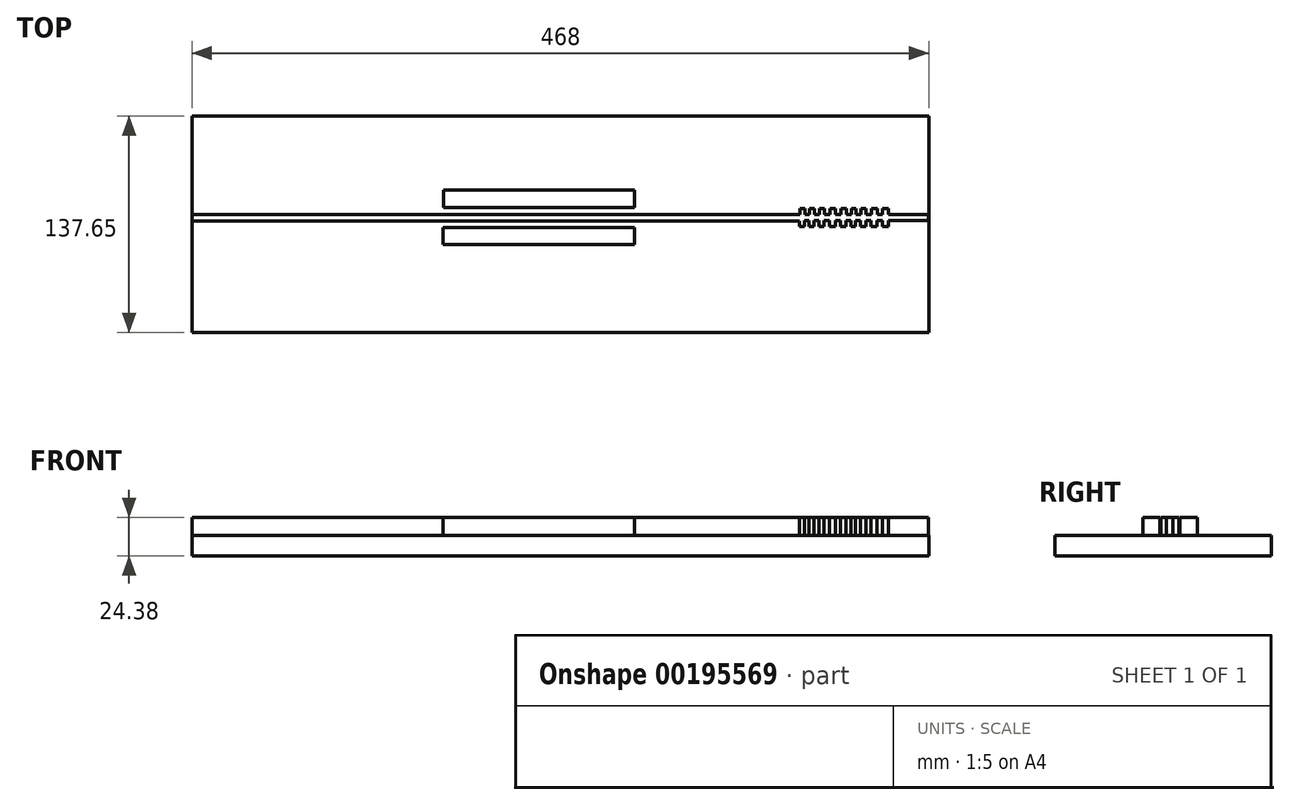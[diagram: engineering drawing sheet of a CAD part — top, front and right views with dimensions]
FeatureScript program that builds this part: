
annotation { "Feature Type Name" : "Feature", "Feature Type Description" : "" }
export const myFeature = defineFeature(function(context is Context, id is Id, definition is map)
    precondition{}
    {
        {
            var Q0;
            Q0=qCreatedBy(makeId("Top.planeOp"),FACE);
            var sketch = newSketch(context, id + "F0", { "sketchPlane" : qUnion([Q0])});
            skLineSegment(sketch, "E0.bottom", {"start": v(-262.44, -29.47) * mm, "end": v(205.56, -29.47) * mm});
            skLineSegment(sketch, "E0.top", {"start": v(-262.44, 108.18) * mm, "end": v(205.56, 108.18) * mm});
            skLineSegment(sketch, "E0.left", {"start": v(-262.44, -29.47) * mm, "end": v(-262.44, 108.18) * mm});
            skLineSegment(sketch, "E0.right", {"start": v(205.56, -29.47) * mm, "end": v(205.56, 108.18) * mm});
            skSolve(sketch);
        }
        {
            var Q0;
            Q0 = qSketchRegion(id + "F0", true);
            extrude(context, id + "F1", {"entities" : qUnion([Q0]), "depth" : 12.95 * mm});
        }
        {
            var Q0;
            Q0=makeQuery(id+"F1.opExtrude","CAP_FACE",FACE,{"disambiguationData":[OSD([sQuery(id+"F0.wireOp",EDGE,"E0.bottom"),sQuery(id+"F0.wireOp",EDGE,"E0.top"),sQuery(id+"F0.wireOp",EDGE,"E0.left"),sQuery(id+"F0.wireOp",EDGE,"E0.right")])],"isStart":false});
            var sketch = newSketch(context, id + "F2", { "sketchPlane" : qUnion([Q0])});
            skLineSegment(sketch, "E1", {"start": v(123.78, 45.55) * mm, "end": v(123.78, 49.46) * mm});
            skLineSegment(sketch, "E2", {"start": v(123.78, 49.46) * mm, "end": v(126.84, 49.46) * mm});
            skLineSegment(sketch, "E3", {"start": v(126.84, 49.46) * mm, "end": v(126.84, 45.7) * mm});
            skLineSegment(sketch, "E4", {"start": v(126.84, 45.7) * mm, "end": v(129.83, 45.7) * mm});
            skLineSegment(sketch, "E5", {"start": v(129.83, 45.7) * mm, "end": v(129.83, 49.46) * mm});
            skLineSegment(sketch, "E6", {"start": v(129.83, 49.46) * mm, "end": v(132.82, 49.46) * mm});
            skLineSegment(sketch, "E7", {"start": v(132.82, 49.46) * mm, "end": v(132.82, 45.7) * mm});
            skLineSegment(sketch, "E8", {"start": v(132.82, 45.7) * mm, "end": v(136.05, 45.7) * mm});
            skLineSegment(sketch, "E9", {"start": v(136.05, 45.7) * mm, "end": v(136.05, 49.46) * mm});
            skLineSegment(sketch, "E10", {"start": v(136.05, 49.46) * mm, "end": v(139.27, 49.46) * mm});
            skLineSegment(sketch, "E11", {"start": v(139.27, 49.46) * mm, "end": v(139.27, 45.7) * mm});
            skLineSegment(sketch, "E12", {"start": v(139.27, 45.7) * mm, "end": v(142.65, 45.7) * mm});
            skLineSegment(sketch, "E13", {"start": v(142.65, 45.7) * mm, "end": v(142.65, 49.46) * mm});
            skLineSegment(sketch, "E14", {"start": v(142.65, 49.46) * mm, "end": v(146.41, 49.46) * mm});
            skLineSegment(sketch, "E15", {"start": v(146.41, 49.46) * mm, "end": v(146.41, 45.7) * mm});
            skLineSegment(sketch, "E16", {"start": v(146.41, 45.7) * mm, "end": v(149.79, 45.7) * mm});
            skLineSegment(sketch, "E17", {"start": v(149.79, 45.7) * mm, "end": v(149.79, 49.46) * mm});
            skLineSegment(sketch, "E18", {"start": v(149.79, 49.46) * mm, "end": v(153.32, 49.46) * mm});
            skLineSegment(sketch, "E19", {"start": v(153.32, 49.46) * mm, "end": v(153.32, 45.7) * mm});
            skLineSegment(sketch, "E20.MirrorCS", {"start": v(126.58, 37.82) * mm, "end": v(126.58, 41.58) * mm});
            skLineSegment(sketch, "E21.MirrorCS", {"start": v(139.02, 41.58) * mm, "end": v(142.4, 41.58) * mm});
            skLineSegment(sketch, "E22.MirrorCS", {"start": v(139.02, 37.82) * mm, "end": v(139.02, 41.58) * mm});
            skLineSegment(sketch, "E23.MirrorCS", {"start": v(129.58, 41.58) * mm, "end": v(129.58, 37.82) * mm});
            skLineSegment(sketch, "E24.MirrorCS", {"start": v(126.58, 41.58) * mm, "end": v(129.58, 41.58) * mm});
            skLineSegment(sketch, "E25.MirrorCS", {"start": v(142.4, 41.58) * mm, "end": v(142.4, 37.82) * mm});
            skLineSegment(sketch, "E26.MirrorCS", {"start": v(129.58, 37.82) * mm, "end": v(132.57, 37.82) * mm});
            skLineSegment(sketch, "E27.MirrorCS", {"start": v(142.4, 37.82) * mm, "end": v(146.16, 37.82) * mm});
            skLineSegment(sketch, "E28.MirrorCS", {"start": v(132.57, 37.82) * mm, "end": v(132.57, 41.58) * mm});
            skLineSegment(sketch, "E29.MirrorCS", {"start": v(132.57, 41.58) * mm, "end": v(135.8, 41.58) * mm});
            skLineSegment(sketch, "E30.MirrorCS", {"start": v(146.16, 37.82) * mm, "end": v(146.16, 41.58) * mm});
            skLineSegment(sketch, "E31.MirrorCS", {"start": v(135.8, 41.58) * mm, "end": v(135.8, 37.82) * mm});
            skLineSegment(sketch, "E32.MirrorCS", {"start": v(123.51, 37.82) * mm, "end": v(126.58, 37.82) * mm});
            skLineSegment(sketch, "E33.MirrorCS", {"start": v(146.16, 41.58) * mm, "end": v(149.54, 41.58) * mm});
            skLineSegment(sketch, "E34.MirrorCS", {"start": v(149.54, 41.58) * mm, "end": v(149.54, 37.82) * mm});
            skLineSegment(sketch, "E35.MirrorCS", {"start": v(135.8, 37.82) * mm, "end": v(139.02, 37.82) * mm});
            skLineSegment(sketch, "E36.MirrorCS", {"start": v(149.54, 37.82) * mm, "end": v(153.07, 37.82) * mm});
            skLineSegment(sketch, "E37.MirrorCS", {"start": v(123.53, 41.51) * mm, "end": v(123.51, 37.82) * mm});
            skLineSegment(sketch, "E38.MirrorCS", {"start": v(153.07, 37.82) * mm, "end": v(153.07, 41.58) * mm});
            skLineSegment(sketch, "E39", {"start": v(153.32, 45.7) * mm, "end": v(156.31, 45.7) * mm});
            skLineSegment(sketch, "E40", {"start": v(156.31, 45.7) * mm, "end": v(156.31, 49.46) * mm});
            skLineSegment(sketch, "E41", {"start": v(156.31, 49.46) * mm, "end": v(159.3, 49.46) * mm});
            skLineSegment(sketch, "E42", {"start": v(159.3, 49.46) * mm, "end": v(159.3, 45.7) * mm});
            skLineSegment(sketch, "E43", {"start": v(159.3, 45.7) * mm, "end": v(162.53, 45.7) * mm});
            skLineSegment(sketch, "E44", {"start": v(162.53, 45.7) * mm, "end": v(162.53, 49.46) * mm});
            skLineSegment(sketch, "E45", {"start": v(162.53, 49.46) * mm, "end": v(165.76, 49.46) * mm});
            skLineSegment(sketch, "E46", {"start": v(165.76, 49.46) * mm, "end": v(165.76, 45.7) * mm});
            skLineSegment(sketch, "E47", {"start": v(165.76, 45.7) * mm, "end": v(169.14, 45.7) * mm});
            skLineSegment(sketch, "E48", {"start": v(169.14, 45.7) * mm, "end": v(169.14, 49.46) * mm});
            skLineSegment(sketch, "E49", {"start": v(169.14, 49.46) * mm, "end": v(172.9, 49.46) * mm});
            skLineSegment(sketch, "E50", {"start": v(172.9, 49.46) * mm, "end": v(172.9, 45.7) * mm});
            skLineSegment(sketch, "E51", {"start": v(172.9, 45.7) * mm, "end": v(176.27, 45.7) * mm});
            skLineSegment(sketch, "E52", {"start": v(176.27, 45.7) * mm, "end": v(176.27, 49.46) * mm});
            skLineSegment(sketch, "E53", {"start": v(176.27, 49.46) * mm, "end": v(179.8, 49.46) * mm});
            skLineSegment(sketch, "E54", {"start": v(179.8, 49.46) * mm, "end": v(179.8, 45.7) * mm});
            skLineSegment(sketch, "E55.MirrorCS", {"start": v(165.5, 41.58) * mm, "end": v(168.88, 41.58) * mm});
            skLineSegment(sketch, "E56.MirrorCS", {"start": v(165.5, 37.82) * mm, "end": v(165.5, 41.58) * mm});
            skLineSegment(sketch, "E57.MirrorCS", {"start": v(156.06, 41.58) * mm, "end": v(156.06, 37.82) * mm});
            skLineSegment(sketch, "E58.MirrorCS", {"start": v(153.07, 41.58) * mm, "end": v(156.06, 41.58) * mm});
            skLineSegment(sketch, "E59.MirrorCS", {"start": v(168.88, 41.58) * mm, "end": v(168.88, 37.82) * mm});
            skLineSegment(sketch, "E60.MirrorCS", {"start": v(156.06, 37.82) * mm, "end": v(159.05, 37.82) * mm});
            skLineSegment(sketch, "E61.MirrorCS", {"start": v(168.88, 37.82) * mm, "end": v(172.64, 37.82) * mm});
            skLineSegment(sketch, "E62.MirrorCS", {"start": v(159.05, 37.82) * mm, "end": v(159.05, 41.58) * mm});
            skLineSegment(sketch, "E63.MirrorCS", {"start": v(159.05, 41.58) * mm, "end": v(162.28, 41.58) * mm});
            skLineSegment(sketch, "E64.MirrorCS", {"start": v(172.64, 37.82) * mm, "end": v(172.64, 41.58) * mm});
            skLineSegment(sketch, "E65.MirrorCS", {"start": v(162.28, 41.58) * mm, "end": v(162.28, 37.82) * mm});
            skLineSegment(sketch, "E66.MirrorCS", {"start": v(172.64, 41.58) * mm, "end": v(176.02, 41.58) * mm});
            skLineSegment(sketch, "E67.MirrorCS", {"start": v(176.02, 41.58) * mm, "end": v(176.02, 37.82) * mm});
            skLineSegment(sketch, "E68.MirrorCS", {"start": v(162.28, 37.82) * mm, "end": v(165.5, 37.82) * mm});
            skLineSegment(sketch, "E69.MirrorCS", {"start": v(176.02, 37.82) * mm, "end": v(179.8, 37.82) * mm});
            skLineSegment(sketch, "E70.MirrorCS", {"start": v(179.8, 37.82) * mm, "end": v(179.8, 41.63) * mm});
            skLineSegment(sketch, "E71", {"start": v(179.8, 45.7) * mm, "end": v(205.45, 45.7) * mm});
            skLineSegment(sketch, "E72", {"start": v(205.45, 45.7) * mm, "end": v(205.45, 41.58) * mm});
            skLineSegment(sketch, "E73", {"start": v(205.45, 41.58) * mm, "end": v(179.8, 41.63) * mm});
            skLineSegment(sketch, "E74", {"start": v(123.78, 45.55) * mm, "end": v(-262.44, 45.55) * mm});
            skLineSegment(sketch, "E75", {"start": v(123.53, 41.51) * mm, "end": v(-262.44, 41.51) * mm});
            skLineSegment(sketch, "E76", {"start": v(-262.44, 41.51) * mm, "end": v(-262.44, 45.55) * mm});
            skLineSegment(sketch, "E77.bottom", {"start": v(-102.48, 60.98) * mm, "end": v(18.7, 60.98) * mm});
            skLineSegment(sketch, "E77.top", {"start": v(-102.48, 50.02) * mm, "end": v(18.7, 50.02) * mm});
            skLineSegment(sketch, "E77.left", {"start": v(-102.48, 60.98) * mm, "end": v(-102.48, 50.02) * mm});
            skLineSegment(sketch, "E77.right", {"start": v(18.7, 60.98) * mm, "end": v(18.7, 50.02) * mm});
            skLineSegment(sketch, "E78.bottom", {"start": v(-103.1, 37.29) * mm, "end": v(18.55, 37.29) * mm});
            skLineSegment(sketch, "E78.top", {"start": v(-103.1, 26.43) * mm, "end": v(18.55, 26.43) * mm});
            skLineSegment(sketch, "E78.left", {"start": v(-103.1, 37.29) * mm, "end": v(-103.1, 26.43) * mm});
            skLineSegment(sketch, "E78.right", {"start": v(18.55, 37.29) * mm, "end": v(18.55, 26.43) * mm});
            skSolve(sketch);
        }
        {
            var Q0;
            Q0 = qSketchRegion(id + "F2", true);
            extrude(context, id + "F3", {"entities" : qUnion([Q0]), "operationType" : NewBodyOperationType.ADD, "depth" : 11.43 * mm});
        }
    });
